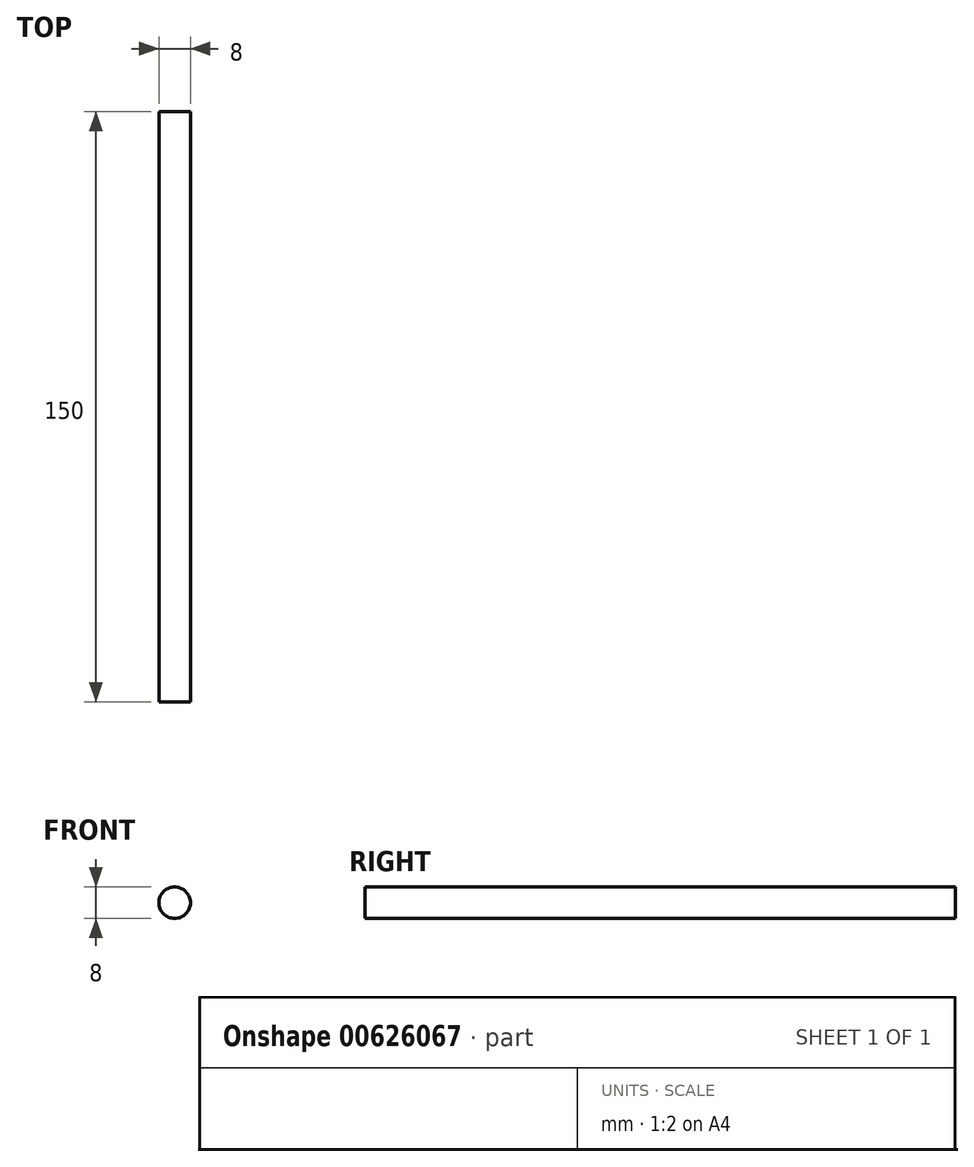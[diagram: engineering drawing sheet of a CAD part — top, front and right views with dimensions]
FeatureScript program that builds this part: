
annotation { "Feature Type Name" : "Feature", "Feature Type Description" : "" }
export const myFeature = defineFeature(function(context is Context, id is Id, definition is map)
    precondition{}
    {
        {
            var Q0;
            Q0=qCreatedBy(makeId("Front.planeOp"),FACE);
            var sketch = newSketch(context, id + "F0", { "sketchPlane" : qUnion([Q0])});
            skCircle(sketch, "E0", {"center": v(0, 0) * mm, "radius": 4 * mm});
            skSolve(sketch);
        }
        {
            var Q0;
            Q0=makeQuery(id+"F0.imprint","IMPRINT",FACE,{"disambiguationData":[TD([[makeQuery(id+"F0.imprint","IMPRINT",EDGE,{"derivedFrom":sQuery(id+"F0.wireOp",EDGE,"E0")}),1.0]])]});
            extrude(context, id + "F1", {"entities" : qUnion([Q0]), "depth" : 150 * mm, "offsetDistance" : 25 * mm});
        }
    });
